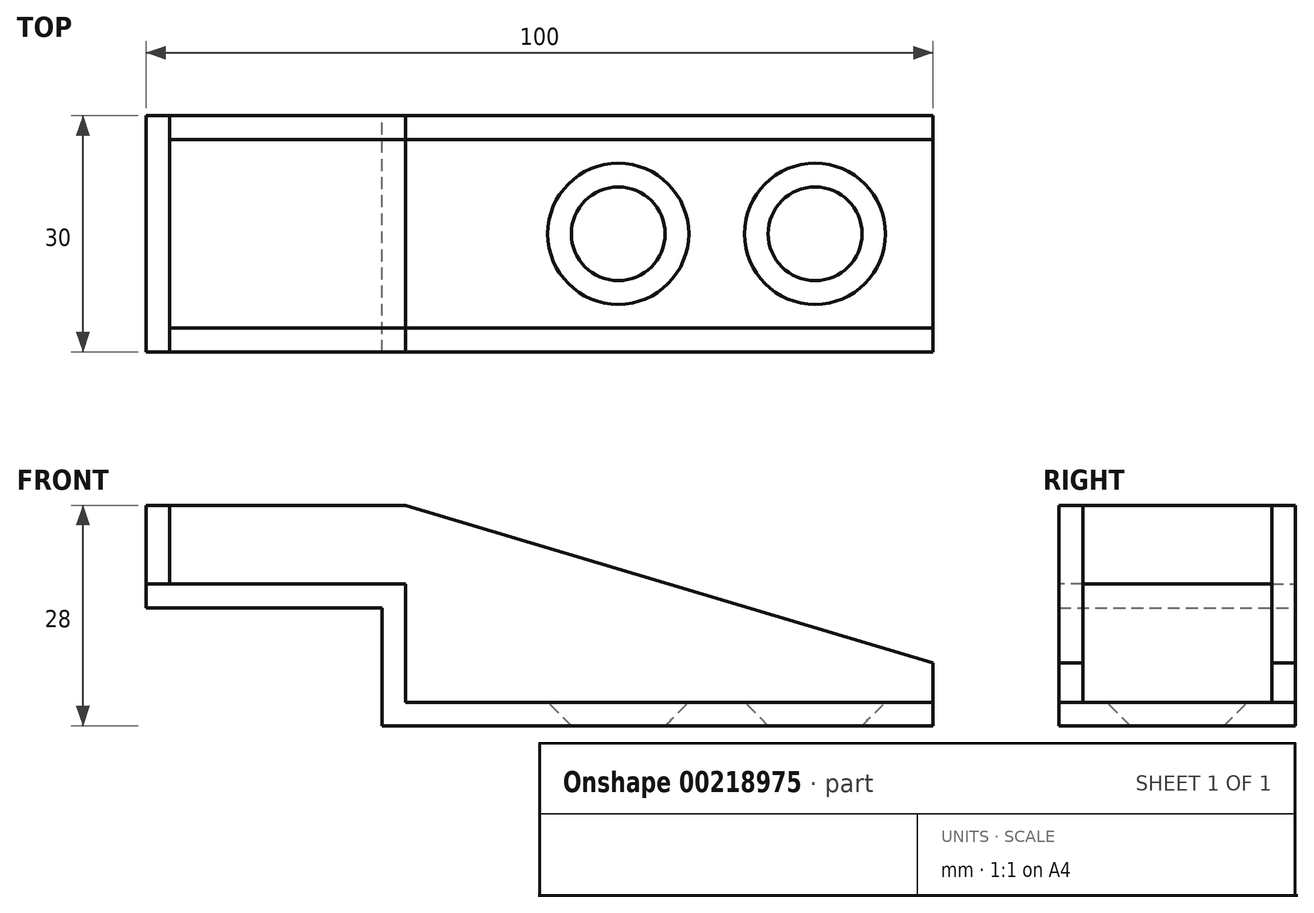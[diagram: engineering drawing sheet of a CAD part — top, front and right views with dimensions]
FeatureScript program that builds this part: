
annotation { "Feature Type Name" : "Feature", "Feature Type Description" : "" }
export const myFeature = defineFeature(function(context is Context, id is Id, definition is map)
    precondition{}
    {
        {
            var Q0;
            Q0=qCreatedBy(makeId("Front.planeOp"),FACE);
            var sketch = newSketch(context, id + "F0", { "sketchPlane" : qUnion([Q0])});
            skLineSegment(sketch, "E0", {"start": v(0, 0) * mm, "end": v(70, 0) * mm});
            skLineSegment(sketch, "E1", {"start": v(70, 0) * mm, "end": v(70, 3) * mm});
            skLineSegment(sketch, "E2", {"start": v(70, 3) * mm, "end": v(3, 3) * mm});
            skLineSegment(sketch, "E3", {"start": v(0, 3) * mm, "end": v(0, 0) * mm});
            skLineSegment(sketch, "E4", {"start": v(0, 3) * mm, "end": v(0, 15) * mm});
            skLineSegment(sketch, "E5", {"start": v(0, 15) * mm, "end": v(-30, 15) * mm});
            skLineSegment(sketch, "E6", {"start": v(-30, 15) * mm, "end": v(-30, 18) * mm});
            skLineSegment(sketch, "E7", {"start": v(-30, 18) * mm, "end": v(3, 18) * mm});
            skLineSegment(sketch, "E8", {"start": v(3, 18) * mm, "end": v(3, 3) * mm});
            skSolve(sketch);
        }
        {
            var Q0;
            Q0=makeQuery(id+"F0.imprint","IMPRINT",FACE,{"disambiguationData":[TD([[makeQuery(id+"F0.imprint","IMPRINT",EDGE,{"derivedFrom":sQuery(id+"F0.wireOp",EDGE,"E0")}),1.0]])]});
            extrude(context, id + "F1", {"entities" : qUnion([Q0]), "endBound" : BoundingType.SYMMETRIC, "depth" : 30 * mm, "offsetDistance" : 25 * mm});
        }
        {
            var Q0;
            Q0=makeQuery(id+"F1.opExtrude","SWEPT_FACE",FACE,{"disambiguationData":[OSD([sQuery(id+"F0.wireOp",EDGE,"E2")])]});
            var sketch = newSketch(context, id + "F2", { "sketchPlane" : qUnion([Q0])});
            skPoint(sketch, "E9", {"position": v(55, 0) * mm});
            skPoint(sketch, "E10", {"position": v(30, 0) * mm});
            skSolve(sketch);
        }
        {
            var Q0;
            Q0=sQuery(id+"F2.wireOp",VERTEX,"E9");
            var Q1;
            Q1=sQuery(id+"F2.wireOp",VERTEX,"E10");
            var Q2;
            Q2=makeQuery(id+"F1.opExtrude","SWEPT_BODY",BODY,{"disambiguationData":[OSD([sQuery(id+"F0.wireOp",EDGE,"E0"),sQuery(id+"F0.wireOp",EDGE,"E1"),sQuery(id+"F0.wireOp",EDGE,"E2"),sQuery(id+"F0.wireOp",EDGE,"E3"),sQuery(id+"F0.wireOp",EDGE,"E4"),sQuery(id+"F0.wireOp",EDGE,"E5"),sQuery(id+"F0.wireOp",EDGE,"E6"),sQuery(id+"F0.wireOp",EDGE,"E7"),sQuery(id+"F0.wireOp",EDGE,"E8")])]});
            hole(context, id + "F3", {"style" : HoleStyle.C_SINK, "endStyle" : HoleEndStyle.THROUGH, "standardTappedOrClearance" : lookupTablePath({ "standard" : "ISO", "fit" : "Normal", "size" : "M8", "type" : "Clearance" }), "standardBlindInLast" : lookupTablePath({ "fit" : "Standard", "standard" : "ISO", "size" : "M8", "type" : "Clearance" }), "holeDiameter" : 8.8 * mm, "cSinkDiameter" : 17.92 * mm, "cSinkAngle" : 90 * degree, "majorDiameter" : 5 * mm, "isTappedThrough" : true, "tappedDepth" : 12 * mm, "tapClearance" : 3, "locations" : qUnion([Q0, Q1]), "scope" : qUnion([Q2])});
        }
        {
            var Q0;
            Q0=makeQuery(id+"F1.opExtrude","SWEPT_FACE",FACE,{"disambiguationData":[OSD([sQuery(id+"F0.wireOp",EDGE,"E7")])]});
            var sketch = newSketch(context, id + "F4", { "sketchPlane" : qUnion([Q0])});
            skLineSegment(sketch, "E11", {"start": v(-30, 15) * mm, "end": v(-30, -15) * mm});
            skLineSegment(sketch, "E12", {"start": v(-30, -15) * mm, "end": v(-27, -15) * mm});
            skLineSegment(sketch, "E13", {"start": v(-27, -15) * mm, "end": v(-27, 15) * mm});
            skLineSegment(sketch, "E14", {"start": v(-27, 15) * mm, "end": v(-30, 15) * mm});
            skSolve(sketch);
        }
        {
            var Q0;
            Q0=makeQuery(id+"F4.imprint","IMPRINT",FACE,{"disambiguationData":[TD([[makeQuery(id+"F4.imprint","IMPRINT",EDGE,{"derivedFrom":sQuery(id+"F4.wireOp",EDGE,"E11")}),-1.0]])]});
            extrude(context, id + "F5", {"entities" : qUnion([Q0]), "depth" : 10 * mm, "offsetDistance" : 25 * mm});
        }
        {
            var Q0;
            Q0=makeQuery(id+"F1.opExtrude","CAP_FACE",FACE,{"disambiguationData":[OSD([sQuery(id+"F0.wireOp",EDGE,"E0"),sQuery(id+"F0.wireOp",EDGE,"E1"),sQuery(id+"F0.wireOp",EDGE,"E2"),sQuery(id+"F0.wireOp",EDGE,"E3"),sQuery(id+"F0.wireOp",EDGE,"E4"),sQuery(id+"F0.wireOp",EDGE,"E5"),sQuery(id+"F0.wireOp",EDGE,"E6"),sQuery(id+"F0.wireOp",EDGE,"E7"),sQuery(id+"F0.wireOp",EDGE,"E8")])],"isStart":false});
            var sketch = newSketch(context, id + "F6", { "sketchPlane" : qUnion([Q0])});
            skLineSegment(sketch, "E15", {"start": v(70, 3) * mm, "end": v(70, 8) * mm});
            skLineSegment(sketch, "E16", {"start": v(-27, 18) * mm, "end": v(-27, 28) * mm});
            skLineSegment(sketch, "E17", {"start": v(-27, 28) * mm, "end": v(3, 28) * mm});
            skLineSegment(sketch, "E18", {"start": v(3, 18) * mm, "end": v(-27, 18) * mm});
            skLineSegment(sketch, "E19", {"start": v(3, 28) * mm, "end": v(70, 8) * mm});
            skLineSegment(sketch, "E20", {"start": v(3, 18) * mm, "end": v(3, 3) * mm});
            skLineSegment(sketch, "E21", {"start": v(3, 3) * mm, "end": v(70, 3) * mm});
            skSolve(sketch);
        }
        {
            var Q0;
            Q0=makeQuery(id+"F1.opExtrude","CAP_FACE",FACE,{"disambiguationData":[OSD([sQuery(id+"F0.wireOp",EDGE,"E0"),sQuery(id+"F0.wireOp",EDGE,"E1"),sQuery(id+"F0.wireOp",EDGE,"E2"),sQuery(id+"F0.wireOp",EDGE,"E3"),sQuery(id+"F0.wireOp",EDGE,"E4"),sQuery(id+"F0.wireOp",EDGE,"E5"),sQuery(id+"F0.wireOp",EDGE,"E6"),sQuery(id+"F0.wireOp",EDGE,"E7"),sQuery(id+"F0.wireOp",EDGE,"E8")])],"isStart":true});
            var sketch = newSketch(context, id + "F7", { "sketchPlane" : qUnion([Q0])});
            skLineSegment(sketch, "E22", {"start": v(27, 18) * mm, "end": v(27, 28) * mm});
            skLineSegment(sketch, "E23", {"start": v(27, 18) * mm, "end": v(-3, 18) * mm});
            skLineSegment(sketch, "E24", {"start": v(-3, 18) * mm, "end": v(-3, 3) * mm});
            skLineSegment(sketch, "E25", {"start": v(-3, 3) * mm, "end": v(-70, 3) * mm});
            skLineSegment(sketch, "E26", {"start": v(-70, 3) * mm, "end": v(-70, 8) * mm});
            skLineSegment(sketch, "E27", {"start": v(-70, 8) * mm, "end": v(-3, 28) * mm});
            skLineSegment(sketch, "E28", {"start": v(27, 28) * mm, "end": v(-3, 28) * mm});
            skSolve(sketch);
        }
        {
            var Q0;
            Q0=makeQuery(id+"F6.imprint","IMPRINT",FACE,{"disambiguationData":[TD([[makeQuery(id+"F6.imprint","IMPRINT",EDGE,{"derivedFrom":sQuery(id+"F6.wireOp",EDGE,"E15")}),1.0]])]});
            extrude(context, id + "F8", {"entities" : qUnion([Q0]), "oppositeDirection" : true, "depth" : 3 * mm, "offsetDistance" : 25 * mm});
        }
        {
            var Q0;
            Q0=makeQuery(id+"F7.imprint","IMPRINT",FACE,{"disambiguationData":[TD([[makeQuery(id+"F7.imprint","IMPRINT",EDGE,{"derivedFrom":sQuery(id+"F7.wireOp",EDGE,"E22")}),1.0]])]});
            extrude(context, id + "F9", {"entities" : qUnion([Q0]), "oppositeDirection" : true, "depth" : 3 * mm, "offsetDistance" : 25 * mm});
        }
    });
